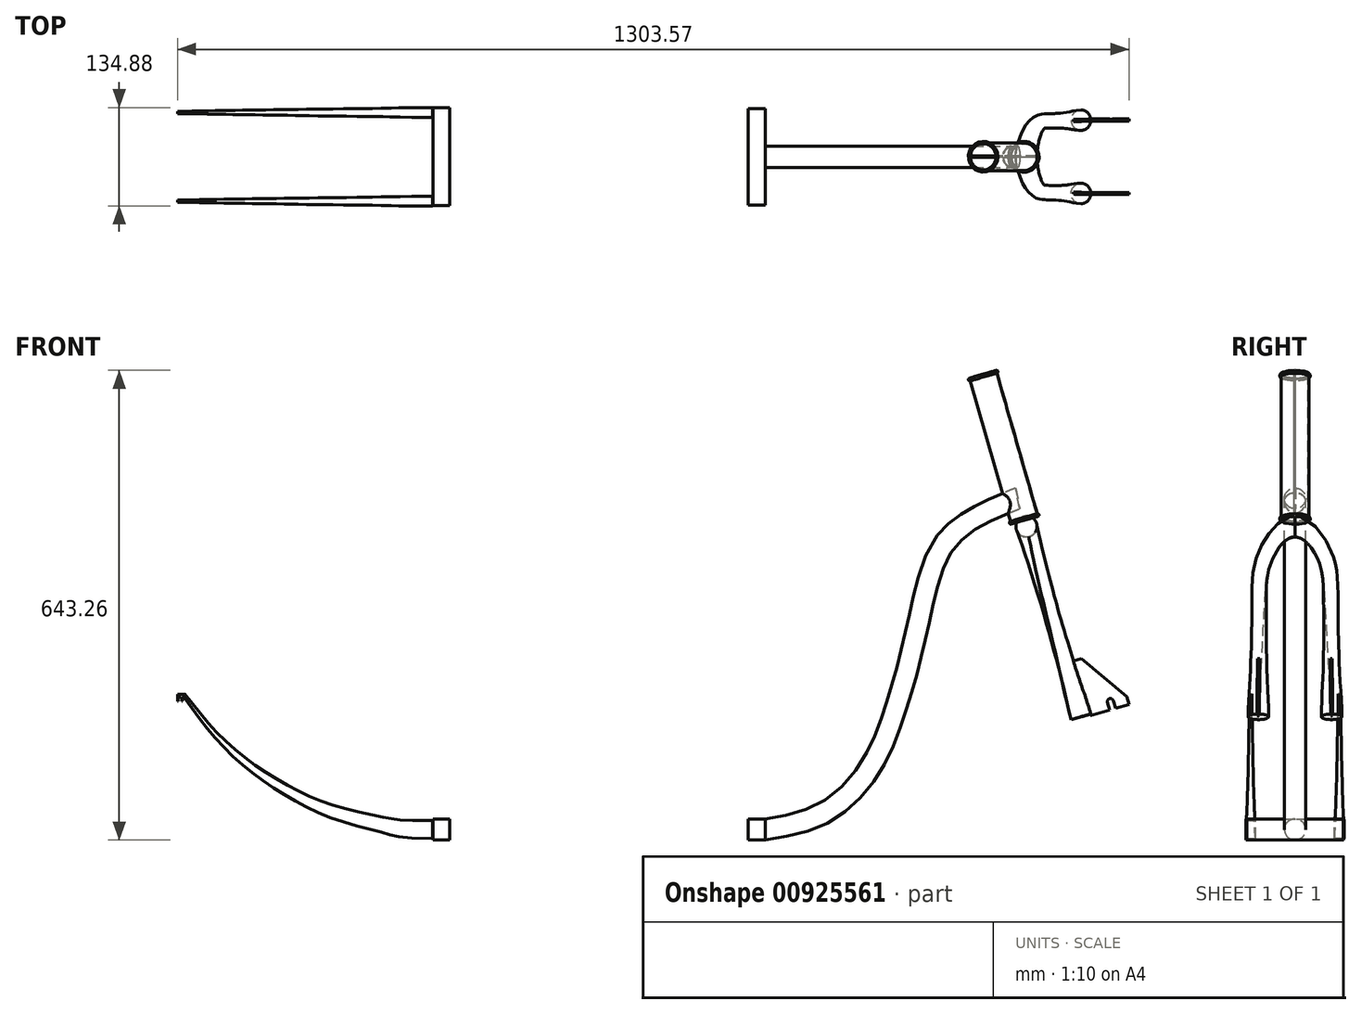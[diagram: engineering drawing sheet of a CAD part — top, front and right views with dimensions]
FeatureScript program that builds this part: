
annotation { "Feature Type Name" : "Feature", "Feature Type Description" : "" }
export const myFeature = defineFeature(function(context is Context, id is Id, definition is map)
    precondition{}
    {
        {
            var Q0;
            Q0=qCreatedBy(makeId("Front.planeOp"),FACE);
            var sketch = newSketch(context, id + "F0", { "sketchPlane" : qUnion([Q0])});
            skLineSegment(sketch, "E0", {"start": v(-47.1, -208.63) * mm, "end": v(-1928.16, -208.63) * mm, "construction": true});
            skLineSegment(sketch, "E1", {"start": v(-47.1, -208.63) * mm, "end": v(222.52, -208.63) * mm, "construction": true});
            skLineSegment(sketch, "E2", {"start": v(-47.1, -208.63) * mm, "end": v(-47.1, 791.37) * mm, "construction": true});
            skLineSegment(sketch, "E3", {"start": v(221.02, -288.63) * mm, "end": v(222.52, -38.63) * mm, "construction": true});
            skLineSegment(sketch, "E4", {"start": v(222.52, -38.63) * mm, "end": v(222.52, 211.37) * mm, "construction": true});
            skCircle(sketch, "E5", {"center": v(222.52, -38.63) * mm, "radius": 250 * mm});
            skLineSegment(sketch, "E6", {"start": v(-231.37, 1373.74) * mm, "end": v(391.94, -800) * mm, "construction": true});
            skLineSegment(sketch, "E7", {"start": v(222.52, -38.63) * mm, "end": v(177.34, -51.59) * mm, "construction": true});
            skSolve(sketch);
        }
        {
            var Q0;
            Q0=qCreatedBy(makeId("Top.planeOp"),FACE);
            cPlane(context, id + "F1", {"entities" : qUnion([Q0]), "cplaneType" : CPlaneType.OFFSET, "offset" : 470 * mm, "width" : 150 * mm, "height" : 150 * mm});
        }
        {
            var Q0;
            Q0=sQuery(id+"F0.wireOp",VERTEX,"E3.end");
            var Q1;
            Q1=qCreatedBy(makeId("Right.planeOp"),FACE);
            cPlane(context, id + "F2", {"entities" : qUnion([Q0, Q1]), "cplaneType" : CPlaneType.PLANE_POINT, "offset" : 251 * mm, "width" : 150 * mm, "height" : 150 * mm});
        }
        {
            var Q0;
            Q0=qCreatedBy(id+"F2.planeOp",FACE);
            var sketch = newSketch(context, id + "F3", { "sketchPlane" : qUnion([Q0])});
            skLineSegment(sketch, "E8", {"start": v(0, -38.63) * mm, "end": v(-50.25, -38.63) * mm, "construction": true});
            skSolve(sketch);
        }
        {
            var Q0;
            Q0=sQuery(id+"F0.wireOp",EDGE,"E6");
            cPlane(context, id + "F4", {"entities" : qUnion([Q0]), "cplaneType" : CPlaneType.LINE_ANGLE, "offset" : 25 * mm, "angle" : 0 * degree, "width" : 150 * mm, "height" : 150 * mm});
        }
        {
            var Q0;
            Q0=qCreatedBy(id+"F4.planeOp",FACE);
            var sketch = newSketch(context, id + "F5", { "sketchPlane" : qUnion([Q0])});
            skLineSegment(sketch, "E9", {"start": v(0, -98.47) * mm, "end": v(140.59, -98.47) * mm, "construction": true});
            skArc(sketch, "E10", {"start": v(48.8, 95.44) * mm, "mid": v(35.42, 141) * mm, "end": v(0, 172.63) * mm});
            skLineSegment(sketch, "E11", {"start": v(0, 181.53) * mm, "end": v(19, 181.53) * mm});
            skArc(sketch, "E12", {"start": v(19, 181.53) * mm, "mid": v(21, 183.53) * mm, "end": v(19, 185.53) * mm});
            skLineSegment(sketch, "E13", {"start": v(19, 185.53) * mm, "end": v(19, 385.53) * mm});
            skArc(sketch, "E14", {"start": v(19, 385.53) * mm, "mid": v(21, 387.53) * mm, "end": v(19, 389.53) * mm});
            skLineSegment(sketch, "E15", {"start": v(19, 389.53) * mm, "end": v(0, 389.53) * mm});
            skLineSegment(sketch, "E16", {"start": v(0, 389.53) * mm, "end": v(0, 181.53) * mm});
            skPoint(sketch, "E17.start.orphan", {"position": v(50.25, -98.47) * mm});
            skLineSegment(sketch, "E18", {"start": v(48.8, 95.44) * mm, "end": v(50.25, -98.47) * mm});
            skSolve(sketch);
        }
        {
            var Q0;
            Q0=makeQuery(id+"F5.imprint","IMPRINT",FACE,{"disambiguationData":[TD([[makeQuery(id+"F5.imprint","IMPRINT",EDGE,{"derivedFrom":sQuery(id+"F5.wireOp",EDGE,"E11")}),1.0]])]});
            var Q1;
            Q1=sQuery(id+"F5.wireOp",EDGE,"E11");
            var Q2;
            Q2=sQuery(id+"F5.wireOp",EDGE,"E12");
            var Q3;
            Q3=sQuery(id+"F5.wireOp",EDGE,"E13");
            var Q4;
            Q4=sQuery(id+"F5.wireOp",EDGE,"E14");
            var Q5;
            Q5=sQuery(id+"F5.wireOp",EDGE,"E15");
            var Q6;
            Q6=sQuery(id+"F5.wireOp",EDGE,"E16");
            var Q7;
            Q7=sQuery(id+"F0.wireOp",EDGE,"E6");
            revolve(context, id + "F6", {"surfaceOperationType" : NewSurfaceOperationType.NEW, "entities" : qUnion([Q0]), "surfaceEntities" : qUnion([Q1, Q2, Q3, Q4, Q5, Q6]), "axis" : qUnion([Q7]), "revolveType" : RevolveType.SYMMETRIC, "angle" : 180 * degree});
        }
        {
            var Q0;
            Q0=makeQuery(id+"F6.opRevolve","SWEPT_FACE",FACE,{"disambiguationData":[OSD([sQuery(id+"F5.wireOp",EDGE,"E15")])]});
            var Q1;
            Q1=makeQuery(id+"F6.opRevolve","SWEPT_FACE",FACE,{"disambiguationData":[OSD([sQuery(id+"F5.wireOp",EDGE,"E11")])]});
            shell(context, id + "F7", {"entities" : qUnion([Q0, Q1]), "thickness" : 1 * mm});
        }
        {
            var Q0;
            Q0=sQuery(id+"F5.wireOp",VERTEX,"E17.start.orphan");
            var Q1;
            Q1=sQuery(id+"F5.wireOp",EDGE,"E18");
            cPlane(context, id + "F8", {"entities" : qUnion([Q0, Q1]), "cplaneType" : CPlaneType.CURVE_POINT, "offset" : 25 * mm, "width" : 150 * mm, "height" : 150 * mm});
        }
        {
            var Q0;
            Q0=qCreatedBy(id+"F8.planeOp",FACE);
            var sketch = newSketch(context, id + "F9", { "sketchPlane" : qUnion([Q0])});
            skCircle(sketch, "E19", {"center": v(156.14, 49.85) * mm, "radius": 14 * mm});
            skSolve(sketch);
        }
        {
            var Q0;
            Q0=qCreatedBy(makeId("Front.planeOp"),FACE);
            var sketch = newSketch(context, id + "F10", { "sketchPlane" : qUnion([Q0])});
            skCircle(sketch, "E20", {"center": v(102.61, 209.01) * mm, "radius": 14.5 * mm});
            skSolve(sketch);
        }
        {
            var Q0;
            Q0=sQuery(id+"F5.wireOp",EDGE,"E18");
            var Q1;
            Q1=sQuery(id+"F5.wireOp",EDGE,"E10");
            var Q3;
            Q3=makeQuery(id+"F9.imprint","IMPRINT",FACE,{"disambiguationData":[TD([[makeQuery(id+"F9.imprint","IMPRINT",EDGE,{"derivedFrom":sQuery(id+"F9.wireOp",EDGE,"E19")}),1.0]])]});
            var Q4;
            Q4=makeQuery(id+"F10.imprint","IMPRINT",FACE,{"disambiguationData":[TD([[makeQuery(id+"F10.imprint","IMPRINT",EDGE,{"derivedFrom":sQuery(id+"F10.wireOp",EDGE,"E20")}),1.0]])]});
            var Q5;
            Q5=sQuery(id+"F9.wireOp",EDGE,"E19");
            var Q6;
            Q6=sQuery(id+"F10.wireOp",EDGE,"E20");
            loft(context, id + "F11", {"addSections" : true, "spine" : qUnion([Q0, Q1]), "sectionCount" : 4, "startCondition" : LoftEndDerivativeType.NORMAL_TO_PROFILE, "startMagnitude" : 1, "endCondition" : LoftEndDerivativeType.NORMAL_TO_PROFILE, "endMagnitude" : 1, "sheetProfilesArray" : [{ "sheetProfileEntities" : qUnion([Q3]) }, { "sheetProfileEntities" : qUnion([Q4]) }], "wireProfilesArray" : [{ "wireProfileEntities" : qUnion([Q5]) }, { "wireProfileEntities" : qUnion([Q6]) }]});
        }
        {
            var Q0;
            Q0=sQuery(id+"F5.wireOp",EDGE,"E18");
            cPlane(context, id + "F12", {"entities" : qUnion([Q0]), "cplaneType" : CPlaneType.LINE_ANGLE, "offset" : 25 * mm, "angle" : 90 * degree, "width" : 150 * mm, "height" : 150 * mm});
        }
        {
            var Q0;
            Q0=qCreatedBy(id+"F12.planeOp",FACE);
            var sketch = newSketch(context, id + "F13", { "sketchPlane" : qUnion([Q0])});
            skLineSegment(sketch, "E21.0", {"start": v(-189.95, -50.5) * mm, "end": v(-166.42, 24.52) * mm});
            skLineSegment(sketch, "E22.0", {"start": v(-166.42, 24.52) * mm, "end": v(-178.3, 27.77) * mm});
            skLineSegment(sketch, "E23.0", {"start": v(-178.3, 27.77) * mm, "end": v(-240.05, -24.25) * mm});
            skLineSegment(sketch, "E24.0", {"start": v(-240.05, -24.25) * mm, "end": v(-243.2, -35.01) * mm});
            skLineSegment(sketch, "E25.0", {"start": v(-213.89, -32.02) * mm, "end": v(-216.98, -42.64) * mm});
            skLineSegment(sketch, "E26", {"start": v(-189.95, -50.5) * mm, "end": v(-216.98, -42.64) * mm});
            skLineSegment(sketch, "E27.trimOffspring", {"start": v(-224.69, -40.42) * mm, "end": v(-221.6, -29.91) * mm});
            skArc(sketch, "E28", {"start": v(-213.89, -32.02) * mm, "mid": v(-216.68, -27.04) * mm, "end": v(-221.6, -29.91) * mm});
            skLineSegment(sketch, "E29", {"start": v(-224.69, -40.42) * mm, "end": v(-243.2, -35.01) * mm});
            skSolve(sketch);
        }
        {
            var Q0;
            Q0=makeQuery(id+"F13.imprint","IMPRINT",FACE,{"disambiguationData":[TD([[makeQuery(id+"F13.imprint","IMPRINT",EDGE,{"derivedFrom":sQuery(id+"F13.wireOp",EDGE,"E21.0")}),1.0]])]});
            extrude(context, id + "F14", {"entities" : qUnion([Q0]), "operationType" : NewBodyOperationType.ADD, "endBound" : BoundingType.SYMMETRIC, "depth" : 3 * mm, "offsetDistance" : 25 * mm});
        }
        {
            var Q0;
            Q0=sQuery(id+"F0.wireOp",EDGE,"E6");
            cPlane(context, id + "F15", {"entities" : qUnion([Q0]), "cplaneType" : CPlaneType.LINE_ANGLE, "offset" : 25 * mm, "angle" : 90 * degree, "width" : 150 * mm, "height" : 150 * mm});
        }
        {
            var Q0;
            Q0=qCreatedBy(id+"F15.planeOp",FACE);
            var sketch = newSketch(context, id + "F16", { "sketchPlane" : qUnion([Q0])});
            skLineSegment(sketch, "E30", {"start": v(-48.62, 399.47) * mm, "end": v(-2.71, 383.4) * mm});
            skSolve(sketch);
        }
        {
            var Q0;
            Q0=qCreatedBy(makeId("Front.planeOp"),FACE);
            cPlane(context, id + "F17", {"entities" : qUnion([Q0]), "cplaneType" : CPlaneType.OFFSET, "offset" : 60.75 * mm, "width" : 150 * mm, "height" : 150 * mm});
        }
        {
            var Q0;
            Q0=qCreatedBy(id+"F17.planeOp",FACE);
            var sketch = newSketch(context, id + "F18", { "sketchPlane" : qUnion([Q0])});
            skLineSegment(sketch, "E31", {"start": v(-261.07, -206) * mm, "end": v(-711.07, -206) * mm});
            skArc(sketch, "E32", {"start": v(-1051.07, -29.15) * mm, "mid": v(-902.69, -159.14) * mm, "end": v(-711.07, -206) * mm});
            skSolve(sketch);
        }
        {
            var Q0;
            Q0=sQuery(id+"F16.wireOp",VERTEX,"E30.start");
            var Q1;
            Q1=sQuery(id+"F18.wireOp",VERTEX,"E31.start");
            var Q2;
            Q2=sQuery(id+"F5.wireOp",VERTEX,"E12.end");
            cPlane(context, id + "F19", {"entities" : qUnion([Q0, Q1, Q2]), "cplaneType" : CPlaneType.THREE_POINT, "offset" : 25 * mm, "width" : 150 * mm, "height" : 150 * mm});
        }
        {
            var Q0;
            Q0=qCreatedBy(id+"F19.planeOp",FACE);
            var sketch = newSketch(context, id + "F20", { "sketchPlane" : qUnion([Q0])});
            skLineSegment(sketch, "E33.0", {"start": v(23.68, 242.48) * mm, "end": v(97.78, -81.3) * mm});
            skLineSegment(sketch, "E34.0", {"start": v(2.15, 353.03) * mm, "end": v(23.68, 242.48) * mm});
            skLineSegment(sketch, "E35.0", {"start": v(-51.3, 393.4) * mm, "end": v(-24.86, 384.2) * mm});
            skArc(sketch, "E36", {"start": v(2.15, 353.03) * mm, "mid": v(-7.2, 372.22) * mm, "end": v(-24.86, 384.2) * mm});
            skArc(sketch, "E37", {"start": v(97.78, -81.3) * mm, "mid": v(156.55, -174.74) * mm, "end": v(260.75, -211.19) * mm});
            skSolve(sketch);
        }
        {
            var Q0;
            Q0=sQuery(id+"F18.wireOp",VERTEX,"E31.end");
            var Q1;
            Q1=sQuery(id+"F18.wireOp",EDGE,"E31");
            cPlane(context, id + "F21", {"entities" : qUnion([Q0, Q1]), "cplaneType" : CPlaneType.CURVE_POINT, "offset" : 25 * mm, "width" : 150 * mm, "height" : 150 * mm});
        }
        {
            var Q0;
            Q0=qCreatedBy(id+"F21.planeOp",FACE);
            var sketch = newSketch(context, id + "F22", { "sketchPlane" : qUnion([Q0])});
            skCircle(sketch, "E38", {"center": v(60.75, -206) * mm, "radius": 14.5 * mm});
            skSolve(sketch);
        }
        {
            var Q0;
            Q0=sQuery(id+"F18.wireOp",VERTEX,"E31.start");
            var Q1;
            Q1=sQuery(id+"F18.wireOp",EDGE,"E31");
            cPlane(context, id + "F23", {"entities" : qUnion([Q0, Q1]), "cplaneType" : CPlaneType.CURVE_POINT, "offset" : 25 * mm, "width" : 150 * mm, "height" : 150 * mm});
        }
        {
            var Q0;
            Q0=qCreatedBy(id+"F23.planeOp",FACE);
            var sketch = newSketch(context, id + "F24", { "sketchPlane" : qUnion([Q0])});
            skCircle(sketch, "E39", {"center": v(60.75, -206) * mm, "radius": 14.5 * mm});
            skSolve(sketch);
        }
        {
            var Q0;
            Q0=sQuery(id+"F20.wireOp",VERTEX,"E33.0.end");
            var Q1;
            Q1=sQuery(id+"F20.wireOp",EDGE,"E37");
            cPlane(context, id + "F25", {"entities" : qUnion([Q0, Q1]), "cplaneType" : CPlaneType.CURVE_POINT, "offset" : 25 * mm, "width" : 150 * mm, "height" : 150 * mm});
        }
        {
            var Q0;
            Q0=qCreatedBy(id+"F25.planeOp",FACE);
            var sketch = newSketch(context, id + "F26", { "sketchPlane" : qUnion([Q0])});
            skCircle(sketch, "E40", {"center": v(-77.52, 40.47) * mm, "radius": 14.5 * mm});
            skSolve(sketch);
        }
        {
            var Q0;
            Q0=sQuery(id+"F20.wireOp",VERTEX,"E33.0.start");
            var Q1;
            Q1=sQuery(id+"F20.wireOp",EDGE,"E33.0");
            cPlane(context, id + "F27", {"entities" : qUnion([Q0, Q1]), "cplaneType" : CPlaneType.CURVE_POINT, "offset" : 25 * mm, "width" : 150 * mm, "height" : 150 * mm});
        }
        {
            var Q0;
            Q0=qCreatedBy(id+"F27.planeOp",FACE);
            var sketch = newSketch(context, id + "F28", { "sketchPlane" : qUnion([Q0])});
            skCircle(sketch, "E41", {"center": v(-77.52, 40.47) * mm, "radius": 14.5 * mm});
            skSolve(sketch);
        }
        {
            var Q0;
            Q0=sQuery(id+"F20.wireOp",VERTEX,"E34.0.start");
            var Q1;
            Q1=sQuery(id+"F20.wireOp",EDGE,"E34.0");
            cPlane(context, id + "F29", {"entities" : qUnion([Q0, Q1]), "cplaneType" : CPlaneType.CURVE_POINT, "offset" : 25 * mm, "width" : 150 * mm, "height" : 150 * mm});
        }
        {
            var Q0;
            Q0=qCreatedBy(id+"F29.planeOp",FACE);
            var sketch = newSketch(context, id + "F30", { "sketchPlane" : qUnion([Q0])});
            skCircle(sketch, "E42", {"center": v(-69.94, 40.54) * mm, "radius": 14.5 * mm});
            skSolve(sketch);
        }
        {
            var Q0;
            Q0=sQuery(id+"F20.wireOp",VERTEX,"E35.0.start");
            var Q1;
            Q1=sQuery(id+"F20.wireOp",EDGE,"E35.0");
            cPlane(context, id + "F31", {"entities" : qUnion([Q0, Q1]), "cplaneType" : CPlaneType.CURVE_POINT, "offset" : 25 * mm, "width" : 150 * mm, "height" : 150 * mm});
        }
        {
            var Q0;
            Q0=qCreatedBy(id+"F31.planeOp",FACE);
            var sketch = newSketch(context, id + "F32", { "sketchPlane" : qUnion([Q0])});
            skCircle(sketch, "E43", {"center": v(5.16, 357.01) * mm, "radius": 14.5 * mm});
            skSolve(sketch);
        }
        {
            var Q0;
            Q0=sQuery(id+"F20.wireOp",EDGE,"E35.0");
            var Q1;
            Q1=sQuery(id+"F20.wireOp",EDGE,"E36");
            var Q2;
            Q2=sQuery(id+"F20.wireOp",EDGE,"E34.0");
            var Q3;
            Q3=sQuery(id+"F32.wireOp",EDGE,"E43");
            var Q4;
            Q4=sQuery(id+"F30.wireOp",EDGE,"E42");
            var Q5;
            Q5=sQuery(id+"F28.wireOp",EDGE,"E41");
            loft(context, id + "F33", {"bodyType" : ToolBodyType.SURFACE, "addSections" : true, "spine" : qUnion([Q0, Q1, Q2]), "sectionCount" : 3, "startCondition" : LoftEndDerivativeType.NORMAL_TO_PROFILE, "startMagnitude" : 0, "endCondition" : LoftEndDerivativeType.NORMAL_TO_PROFILE, "endMagnitude" : 0, "wireProfilesArray" : [{ "wireProfileEntities" : qUnion([Q3]) }, { "wireProfileEntities" : qUnion([Q4]) }, { "wireProfileEntities" : qUnion([Q5]) }]});
        }
        {
            var Q0;
            Q0=sQuery(id+"F20.wireOp",EDGE,"E33.0");
            var Q1;
            Q1=sQuery(id+"F26.wireOp",EDGE,"E40");
            var Q2;
            Q2=makeQuery(id+"F33.opLoft","MID_CAP_EDGE",EDGE,{"disambiguationData":[OSD([sQuery(id+"F28.wireOp",EDGE,"E41")])],"capPos":2.0});
            loft(context, id + "F34", {"bodyType" : ToolBodyType.SURFACE, "surfaceOperationType" : NewSurfaceOperationType.ADD, "addSections" : true, "spine" : qUnion([Q0]), "sectionCount" : 5, "wireProfilesArray" : [{ "wireProfileEntities" : qUnion([Q1]) }, { "wireProfileEntities" : qUnion([Q2]) }]});
        }
        {
            var Q0;
            Q0=sQuery(id+"F20.wireOp",EDGE,"E37");
            var Q1;
            Q1=sQuery(id+"F24.wireOp",EDGE,"E39");
            var Q2;
            Q2=makeQuery(id+"F34.opLoft","MID_CAP_EDGE",EDGE,{"disambiguationData":[OSD([sQuery(id+"F26.wireOp",EDGE,"E40")])],"capPos":0.0});
            loft(context, id + "F35", {"bodyType" : ToolBodyType.SURFACE, "surfaceOperationType" : NewSurfaceOperationType.ADD, "addSections" : true, "spine" : qUnion([Q0]), "sectionCount" : 8, "startCondition" : LoftEndDerivativeType.NORMAL_TO_PROFILE, "startMagnitude" : 0, "endCondition" : LoftEndDerivativeType.MATCH_CURVATURE, "endMagnitude" : 0, "wireProfilesArray" : [{ "wireProfileEntities" : qUnion([Q1]) }, { "wireProfileEntities" : qUnion([Q2]) }]});
        }
        {
            var Q0;
            Q0=sQuery(id+"F18.wireOp",EDGE,"E31");
            var Q1;
            Q1=makeQuery(id+"F35.opLoft","MID_CAP_EDGE",EDGE,{"disambiguationData":[OSD([sQuery(id+"F24.wireOp",EDGE,"E39")])],"capPos":0.0});
            var Q2;
            Q2=sQuery(id+"F22.wireOp",EDGE,"E38");
            loft(context, id + "F36", {"bodyType" : ToolBodyType.SURFACE, "surfaceOperationType" : NewSurfaceOperationType.ADD, "addSections" : true, "spine" : qUnion([Q0]), "sectionCount" : 5, "wireProfilesArray" : [{ "wireProfileEntities" : qUnion([Q1]) }, { "wireProfileEntities" : qUnion([Q2]) }]});
        }
        {
            var Q0;
            Q0=qCreatedBy(id+"F21.planeOp",FACE);
            var sketch = newSketch(context, id + "F37", { "sketchPlane" : qUnion([Q0])});
            skLineSegment(sketch, "E44.bottom", {"start": v(67.44, -218.2) * mm, "end": v(54.06, -218.2) * mm});
            skLineSegment(sketch, "E44.top", {"start": v(67.44, -193.78) * mm, "end": v(54.06, -193.78) * mm});
            skLineSegment(sketch, "E44.left", {"start": v(67.44, -218.2) * mm, "end": v(67.44, -193.78) * mm});
            skLineSegment(sketch, "E44.right", {"start": v(54.06, -218.2) * mm, "end": v(54.06, -193.78) * mm});
            skPoint(sketch, "E44.middle", {"position": v(60.75, -206) * mm});
            skSolve(sketch);
        }
        {
            var Q0;
            Q0=qCreatedBy(makeId("Front.planeOp"),FACE);
            var Q1;
            Q1=sQuery(id+"F18.wireOp",VERTEX,"E32.start");
            cPlane(context, id + "F38", {"entities" : qUnion([Q0, Q1]), "cplaneType" : CPlaneType.PLANE_POINT, "offset" : 25 * mm, "width" : 150 * mm, "height" : 150 * mm});
        }
        {
            var Q0;
            Q0=qCreatedBy(id+"F38.planeOp",FACE);
            var sketch = newSketch(context, id + "F39", { "sketchPlane" : qUnion([Q0])});
            skLineSegment(sketch, "E45.left", {"start": v(-1054.76, -27.42) * mm, "end": v(-1054.76, -30.31) * mm});
            skLineSegment(sketch, "E45.right", {"start": v(-1059.9, -27.42) * mm, "end": v(-1059.9, -30.31) * mm});
            skPoint(sketch, "E45.middle", {"position": v(-1057.33, -28.93) * mm});
            skArc(sketch, "E46", {"start": v(-1054.76, -27.42) * mm, "mid": v(-1057.33, -24.85) * mm, "end": v(-1059.9, -27.42) * mm});
            skLineSegment(sketch, "E47", {"start": v(-1059.9, -30.31) * mm, "end": v(-1060.46, -30.31) * mm});
            skLineSegment(sketch, "E48", {"start": v(-1060.46, -30.31) * mm, "end": v(-1060.46, -21.08) * mm});
            skLineSegment(sketch, "E49", {"start": v(-1060.46, -21.08) * mm, "end": v(-1050.43, -21.08) * mm});
            skLineSegment(sketch, "E50", {"start": v(-1050.43, -21.08) * mm, "end": v(-1051.34, -24.31) * mm});
            skLineSegment(sketch, "E51", {"start": v(-1051.34, -24.31) * mm, "end": v(-1054.25, -24.31) * mm});
            skLineSegment(sketch, "E52", {"start": v(-1054.25, -24.31) * mm, "end": v(-1054.25, -30.31) * mm});
            skLineSegment(sketch, "E53", {"start": v(-1054.25, -30.31) * mm, "end": v(-1054.76, -30.31) * mm});
            skSolve(sketch);
        }
        {
            var Q0;
            Q0=sQuery(id+"F39.wireOp",EDGE,"E50");
            cPoint(context, id + "F40", {"entities" : qUnion([Q0]), "parameter" : 0.5});
        }
        {
            var Q0;
            Q0 = qCreatedBy(id + "F40" ,VERTEX);
            var Q1;
            Q1=sQuery(id+"F39.wireOp",EDGE,"E49");
            cPlane(context, id + "F41", {"entities" : qUnion([Q0, Q1]), "cplaneType" : CPlaneType.CURVE_POINT, "offset" : 25 * mm, "width" : 150 * mm, "height" : 150 * mm});
        }
        {
            var Q0;
            Q0=qCreatedBy(id+"F41.planeOp",FACE);
            var sketch = newSketch(context, id + "F42", { "sketchPlane" : qUnion([Q0])});
            skLineSegment(sketch, "E54.bottom", {"start": v(-62.25, -19.9) * mm, "end": v(-59.25, -19.9) * mm});
            skLineSegment(sketch, "E54.top", {"start": v(-62.25, -25.9) * mm, "end": v(-59.25, -25.9) * mm});
            skLineSegment(sketch, "E54.left", {"start": v(-62.25, -19.9) * mm, "end": v(-62.25, -25.9) * mm});
            skLineSegment(sketch, "E54.right", {"start": v(-59.25, -19.9) * mm, "end": v(-59.25, -25.9) * mm});
            skPoint(sketch, "E54.middle", {"position": v(-60.75, -22.9) * mm});
            skSolve(sketch);
        }
        {
            var Q0;
            Q0=makeQuery(id+"F39.imprint","IMPRINT",FACE,{"disambiguationData":[TD([[makeQuery(id+"F39.imprint","IMPRINT",EDGE,{"derivedFrom":sQuery(id+"F39.wireOp",EDGE,"E45.left")}),1.0]])]});
            extrude(context, id + "F43", {"entities" : qUnion([Q0]), "endBound" : BoundingType.SYMMETRIC, "depth" : 3 * mm, "offsetDistance" : 25 * mm});
        }
        {
            var Q0;
            Q0=sQuery(id+"F18.wireOp",EDGE,"E32");
            var Q2;
            Q2=makeQuery(id+"F37.imprint","IMPRINT",FACE,{"disambiguationData":[TD([[makeQuery(id+"F37.imprint","IMPRINT",EDGE,{"derivedFrom":sQuery(id+"F37.wireOp",EDGE,"E44.bottom")}),-1.0]])]});
            var Q3;
            Q3=makeQuery(id+"F42.imprint","IMPRINT",FACE,{"disambiguationData":[TD([[makeQuery(id+"F42.imprint","IMPRINT",EDGE,{"derivedFrom":sQuery(id+"F42.wireOp",EDGE,"E54.bottom")}),-1.0]])]});
            loft(context, id + "F44", {"operationType" : NewBodyOperationType.ADD, "addSections" : true, "spine" : qUnion([Q0]), "sectionCount" : 5, "startCondition" : LoftEndDerivativeType.NORMAL_TO_PROFILE, "startMagnitude" : 2, "sheetProfilesArray" : [{ "sheetProfileEntities" : qUnion([Q2]) }, { "sheetProfileEntities" : qUnion([Q3]) }]});
        }
        {
            var Q0;
            Q0=qCreatedBy(makeId("Front.planeOp"),FACE);
            var sketch = newSketch(context, id + "F45", { "sketchPlane" : qUnion([Q0])});
            skCircle(sketch, "E55", {"center": v(-1057.73, -28.3) * mm, "radius": 250 * mm});
            skSolve(sketch);
        }
        {
            var Q0;
            Q0=makeQuery(id+"F6.opRevolve","SWEPT_BODY",BODY,{"disambiguationData":[OSD([sQuery(id+"F5.wireOp",EDGE,"E11"),sQuery(id+"F5.wireOp",EDGE,"E12"),sQuery(id+"F5.wireOp",EDGE,"E13"),sQuery(id+"F5.wireOp",EDGE,"E14"),sQuery(id+"F5.wireOp",EDGE,"E15"),sQuery(id+"F5.wireOp",EDGE,"E16")])]});
            var Q1;
            Q1=makeQuery(id+"F11.opLoft","SWEPT_BODY",BODY,{"disambiguationData":[OSD([makeQuery(id+"F9.imprint","IMPRINT",FACE,{"disambiguationData":[TD([[makeQuery(id+"F9.imprint","IMPRINT",EDGE,{"derivedFrom":sQuery(id+"F9.wireOp",EDGE,"E19")}),1.0]])]}),makeQuery(id+"F10.imprint","IMPRINT",FACE,{"disambiguationData":[TD([[makeQuery(id+"F10.imprint","IMPRINT",EDGE,{"derivedFrom":sQuery(id+"F10.wireOp",EDGE,"E20")}),1.0]])]})])]});
            var Q2;
            Q2=makeQuery(id+"F43.opExtrude","SWEPT_BODY",BODY,{"disambiguationData":[OSD([sQuery(id+"F39.wireOp",EDGE,"E45.left"),sQuery(id+"F39.wireOp",EDGE,"E45.right"),sQuery(id+"F39.wireOp",EDGE,"E46"),sQuery(id+"F39.wireOp",EDGE,"E47"),sQuery(id+"F39.wireOp",EDGE,"E48"),sQuery(id+"F39.wireOp",EDGE,"E49"),sQuery(id+"F39.wireOp",EDGE,"E50"),sQuery(id+"F39.wireOp",EDGE,"E51"),sQuery(id+"F39.wireOp",EDGE,"E52"),sQuery(id+"F39.wireOp",EDGE,"E53")])]});
            var Q3;
            Q3=makeQuery(id+"F33.opLoft","SWEPT_BODY",BODY,{"disambiguationData":[OSD([sQuery(id+"F28.wireOp",EDGE,"E41"),sQuery(id+"F30.wireOp",EDGE,"E42"),sQuery(id+"F32.wireOp",EDGE,"E43")])]});
            var Q4;
            Q4=makeQuery(id+"F45.imprint","IMPRINT",FACE,{"disambiguationData":[TD([[makeQuery(id+"F45.imprint","IMPRINT",EDGE,{"derivedFrom":sQuery(id+"F45.wireOp",EDGE,"E55")}),1.0]])]});
            mirror(context, id + "F46", {"entities" : qUnion([Q0, Q1, Q2, Q3]), "mirrorPlane" : qUnion([Q4])});
        }
        {
            var Q0;
            Q0=qCreatedBy(makeId("Front.planeOp"),FACE);
            var sketch = newSketch(context, id + "F47", { "sketchPlane" : qUnion([Q0])});
            skFitSpline(sketch, "E56", {"points": [v(90.55, 247.51) * mm, v(0, 197.36) * mm, v(-26.59, 148.2) * mm, v(-65.4, 0) * mm, v(-98.82, -99.11) * mm, v(-135.67, -152.49) * mm, v(-172.16, -181.36) * mm, v(-212.1, -199.8) * mm, v(-260.33, -205.94) * mm], "startDerivative": vector(-797.05, -166.98) * mm, "endDerivative": vector(-401.93, 16.98) * mm});
            skSolve(sketch);
        }
        {
            var Q0;
            Q0=qCreatedBy(makeId("Right.planeOp"),FACE);
            cPlane(context, id + "F48", {"entities" : qUnion([Q0]), "cplaneType" : CPlaneType.OFFSET, "offset" : 256 * mm, "oppositeDirection" : true, "width" : 150 * mm, "height" : 150 * mm});
        }
        {
            var Q0;
            Q0=qCreatedBy(id+"F48.planeOp",FACE);
            var sketch = newSketch(context, id + "F49", { "sketchPlane" : qUnion([Q0])});
            skCircle(sketch, "E57", {"center": v(0, -205.94) * mm, "radius": 14.5 * mm});
            skSolve(sketch);
        }
        {
            var Q0;
            Q0=sQuery(id+"F47.wireOp",VERTEX,"E56.start");
            var Q1;
            Q1=sQuery(id+"F47.wireOp",EDGE,"E56");
            cPlane(context, id + "F50", {"entities" : qUnion([Q0, Q1]), "cplaneType" : CPlaneType.CURVE_POINT, "offset" : 25 * mm, "width" : 150 * mm, "height" : 150 * mm});
        }
        {
            var Q0;
            Q0=qCreatedBy(id+"F50.planeOp",FACE);
            var sketch = newSketch(context, id + "F51", { "sketchPlane" : qUnion([Q0])});
            skCircle(sketch, "E58", {"center": v(0, 223.69) * mm, "radius": 14.5 * mm});
            skSolve(sketch);
        }
        {
            var Q0;
            Q0=sQuery(id+"F47.wireOp",EDGE,"E56");
            var Q2;
            Q2=makeQuery(id+"F49.imprint","IMPRINT",FACE,{"disambiguationData":[TD([[makeQuery(id+"F49.imprint","IMPRINT",EDGE,{"derivedFrom":sQuery(id+"F49.wireOp",EDGE,"E57")}),1.0]])]});
            var Q3;
            Q3=makeQuery(id+"F51.imprint","IMPRINT",FACE,{"disambiguationData":[TD([[makeQuery(id+"F51.imprint","IMPRINT",EDGE,{"derivedFrom":sQuery(id+"F51.wireOp",EDGE,"E58")}),1.0]])]});
            loft(context, id + "F52", {"operationType" : NewBodyOperationType.ADD, "addSections" : true, "spine" : qUnion([Q0]), "sectionCount" : 5, "sheetProfilesArray" : [{ "sheetProfileEntities" : qUnion([Q2]) }, { "sheetProfileEntities" : qUnion([Q3]) }]});
        }
        {
            var Q0;
            Q0=qCreatedBy(makeId("Front.planeOp"),FACE);
            var sketch = newSketch(context, id + "F53", { "sketchPlane" : qUnion([Q0])});
            skLineSegment(sketch, "E59.bottom", {"start": v(-255.33, -220.44) * mm, "end": v(-278.57, -220.44) * mm});
            skLineSegment(sketch, "E59.top", {"start": v(-255.33, -191.44) * mm, "end": v(-278.57, -191.44) * mm});
            skLineSegment(sketch, "E59.left", {"start": v(-255.33, -220.44) * mm, "end": v(-255.33, -191.44) * mm});
            skLineSegment(sketch, "E59.right", {"start": v(-278.57, -220.44) * mm, "end": v(-278.57, -191.44) * mm});
            skPoint(sketch, "E59.middle", {"position": v(-266.95, -205.94) * mm});
            skLineSegment(sketch, "E60.bottom", {"start": v(-687.44, -220.44) * mm, "end": v(-710.67, -220.44) * mm});
            skLineSegment(sketch, "E60.top", {"start": v(-687.44, -191.44) * mm, "end": v(-710.67, -191.44) * mm});
            skLineSegment(sketch, "E60.left", {"start": v(-687.44, -220.44) * mm, "end": v(-687.44, -191.44) * mm});
            skLineSegment(sketch, "E60.right", {"start": v(-710.67, -220.44) * mm, "end": v(-710.67, -191.44) * mm});
            skPoint(sketch, "E60.middle", {"position": v(-699.05, -205.94) * mm});
            skSolve(sketch);
        }
        {
            var Q0;
            Q0=makeQuery(id+"F53.imprint","IMPRINT",FACE,{"disambiguationData":[TD([[makeQuery(id+"F53.imprint","IMPRINT",EDGE,{"derivedFrom":sQuery(id+"F53.wireOp",EDGE,"E59.bottom")}),-1.0]])]});
            var Q1;
            Q1=makeQuery(id+"F36.opLoft","SWEPT_FACE",FACE,{"disambiguationData":[OSD([sQuery(id+"F22.wireOp",EDGE,"E38"),sQuery(id+"F24.wireOp",EDGE,"E39")])]});
            extrude(context, id + "F54", {"entities" : qUnion([Q0]), "endBound" : BoundingType.SYMMETRIC, "depth" : 132 * mm, "endBoundEntityFace" : qUnion([Q1]), "offsetDistance" : 25 * mm});
        }
        {
            var Q0;
            Q0=makeQuery(id+"F53.imprint","IMPRINT",FACE,{"disambiguationData":[TD([[makeQuery(id+"F53.imprint","IMPRINT",EDGE,{"derivedFrom":sQuery(id+"F53.wireOp",EDGE,"E60.bottom")}),-1.0]])]});
            extrude(context, id + "F55", {"entities" : qUnion([Q0]), "operationType" : NewBodyOperationType.ADD, "endBound" : BoundingType.SYMMETRIC, "depth" : 134 * mm, "offsetDistance" : 25 * mm});
        }
    });
